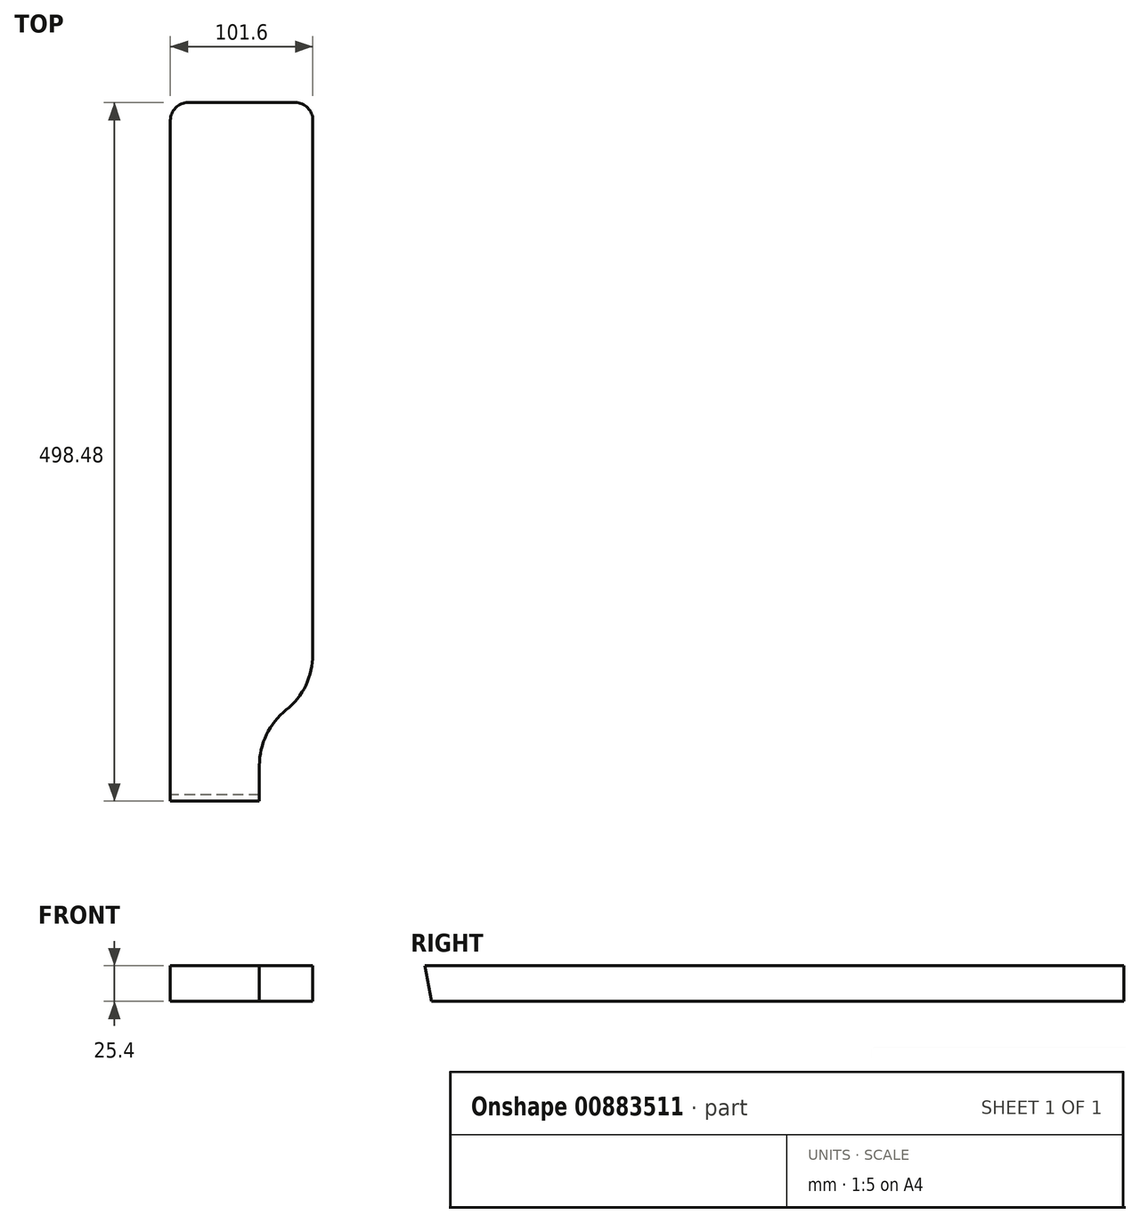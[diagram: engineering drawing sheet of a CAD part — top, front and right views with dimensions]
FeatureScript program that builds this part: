
annotation { "Feature Type Name" : "Feature", "Feature Type Description" : "" }
export const myFeature = defineFeature(function(context is Context, id is Id, definition is map)
    precondition{}
    {
        {
            var Q0;
            Q0=qCreatedBy(makeId("Top.planeOp"),FACE);
            var sketch = newSketch(context, id + "F0", { "sketchPlane" : qUnion([Q0])});
            skLineSegment(sketch, "E0.bottom", {"start": v(0, 0) * mm, "end": v(63.5, 0) * mm});
            skLineSegment(sketch, "E0.top", {"start": v(12.7, 498.48) * mm, "end": v(88.9, 498.48) * mm});
            skLineSegment(sketch, "E0.left", {"start": v(0, 0) * mm, "end": v(0, 485.77) * mm});
            skLineSegment(sketch, "E0.right", {"start": v(101.6, 0) * mm, "end": v(101.6, 104.71) * mm, "construction": true});
            skLineSegment(sketch, "E1", {"start": v(101.6, 104.71) * mm, "end": v(101.6, 485.78) * mm});
            skLineSegment(sketch, "E2", {"start": v(63.5, 0) * mm, "end": v(101.6, 0) * mm, "construction": true});
            skLineSegment(sketch, "E3", {"start": v(63.5, 0) * mm, "end": v(63.5, 25.4) * mm});
            skArc(sketch, "E4", {"start": v(63.5, 25.4) * mm, "mid": v(68.5, 47.4) * mm, "end": v(82.55, 65.06) * mm});
            skArc(sketch, "E5", {"start": v(82.55, 65.06) * mm, "mid": v(96.6, 82.71) * mm, "end": v(101.6, 104.71) * mm});
            skPoint(sketch, "E6.visualSharp", {"position": v(101.6, 498.48) * mm});
            skArc(sketch, "E6.filletArc", {"start": v(101.6, 485.78) * mm, "mid": v(97.88, 494.76) * mm, "end": v(88.9, 498.48) * mm});
            skPoint(sketch, "E7.visualSharp", {"position": v(0, 498.48) * mm});
            skArc(sketch, "E7.filletArc", {"start": v(12.7, 498.48) * mm, "mid": v(3.72, 494.76) * mm, "end": v(0, 485.78) * mm});
            skSolve(sketch);
        }
        {
            var Q0;
            Q0 = qSketchRegion(id + "F0", true);
            extrude(context, id + "F1", {"entities" : qUnion([Q0]), "depth" : 25.4 * mm, "offsetDistance" : 25.4 * mm});
        }
        {
            var Q0;
            Q0=makeQuery(id+"F1.opExtrude","CAP_EDGE",EDGE,{"disambiguationData":[OSD([sQuery(id+"F0.wireOp",EDGE,"E0.bottom")])],"isStart":true});
            chamfer(context, id + "F2", {"entities" : qUnion([Q0]), "chamferType" : ChamferType.OFFSET_ANGLE, "width" : 25.4 * mm, "oppositeDirection" : false, "angle" : 10 * degree, "tangentPropagation" : true});
        }
    });
